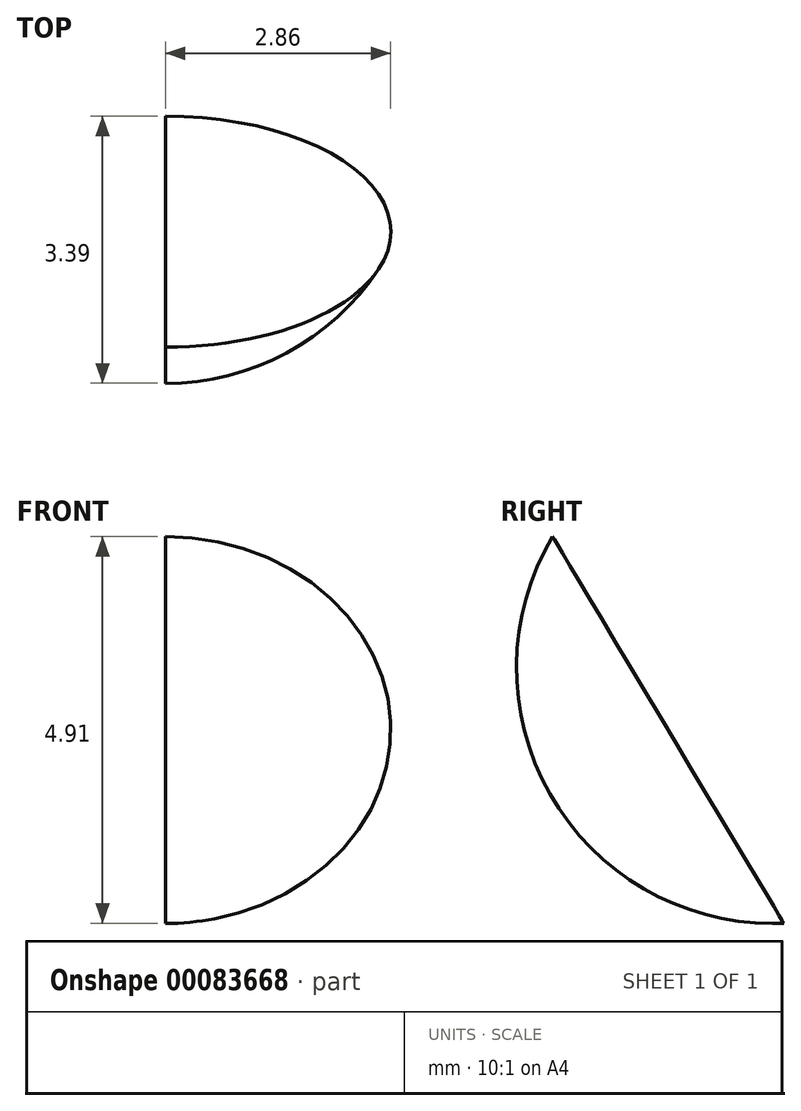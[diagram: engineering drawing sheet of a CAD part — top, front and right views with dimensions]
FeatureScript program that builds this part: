
annotation { "Feature Type Name" : "Feature", "Feature Type Description" : "" }
export const myFeature = defineFeature(function(context is Context, id is Id, definition is map)
    precondition{}
    {
        {
            var Q0;
            Q0=qCreatedBy(makeId("Right.planeOp"),FACE);
            var sketch = newSketch(context, id + "F0", { "sketchPlane" : qUnion([Q0])});
            skArc(sketch, "E0", {"start": v(0, 52.08) * mm, "mid": v(3.25, 55.33) * mm, "end": v(0, 58.58) * mm});
            skLineSegment(sketch, "E1", {"start": v(1.56, 52.48) * mm, "end": v(10.9, 19.74) * mm});
            skLineSegment(sketch, "E2", {"start": v(0, 19.74) * mm, "end": v(0, 55.33) * mm});
            skLineSegment(sketch, "E3", {"start": v(0, 55.33) * mm, "end": v(0, 69.72) * mm});
            skLineSegment(sketch, "E4", {"start": v(10.9, 19.74) * mm, "end": v(0, 19.74) * mm});
            skPoint(sketch, "E5.orphan", {"position": v(16.55, 0) * mm});
            skSolve(sketch);
        }
        {
            var Q0;
            {var subQ3=sQuery(id+"F0.wireOp",EDGE,"E1");Q0=makeQuery(id+"F0.imprint","IMPRINT",FACE,{"disambiguationData":[TD([[makeQuery(id+"F0.imprint","IMPRINT",EDGE,{"derivedFrom":subQ3}),-1.0]])]});}
            var Q1;
            {var subQ0=sQuery(id+"F0.wireOp",EDGE,"E2");var subQ1=sQuery(id+"F0.wireOp",EDGE,"E0");var subQ2=makeQuery(id+"F0.imprint","INTERSECT",VERTEX,{"derivedFrom":[subQ1,subQ0]});Q1=makeQuery(id+"F0.imprint","IMPRINT",FACE,{"disambiguationData":[TD([[makeQuery(id+"F0.imprint","IMPRINT",EDGE,{"disambiguationData":[TD([[subQ2,-1.0]])],"derivedFrom":subQ1}),1.0]])]});}
            var Q2;
            Q2=sQuery(id+"F0.wireOp",EDGE,"E3");
            revolve(context, id + "F1", {"entities" : qUnion([Q0, Q1]), "axis" : qUnion([Q2]), "revolveType" : RevolveType.FULL});
        }
        {
            var Q0;
            Q0=qCreatedBy(makeId("Right.planeOp"),FACE);
            var sketch = newSketch(context, id + "F2", { "sketchPlane" : qUnion([Q0])});
            skLineSegment(sketch, "E6", {"start": v(-6.62, 63.4) * mm, "end": v(15.64, 26.15) * mm});
            skLineSegment(sketch, "E7", {"start": v(11.15, 27.52) * mm, "end": v(-9.42, 62) * mm});
            skLineSegment(sketch, "E8", {"start": v(-9.42, 62) * mm, "end": v(-6.62, 63.4) * mm});
            skLineSegment(sketch, "E9", {"start": v(15.64, 26.15) * mm, "end": v(11.15, 27.52) * mm});
            skSolve(sketch);
        }
        {
            var Q0;
            Q0=makeQuery(id+"F2.imprint","IMPRINT",FACE,{"disambiguationData":[TD([[makeQuery(id+"F2.imprint","IMPRINT",EDGE,{"derivedFrom":sQuery(id+"F2.wireOp",EDGE,"E6")}),-1.0]])]});
            var Q1;
            Q1=sQuery(id+"F2.wireOp",EDGE,"E8");
            extrude(context, id + "F3", {"entities" : qUnion([Q0]), "operationType" : NewBodyOperationType.REMOVE, "surfaceEntities" : qUnion([Q1]), "endBound" : BoundingType.THROUGH_ALL, "depth" : 1 * mm});
        }
    });
